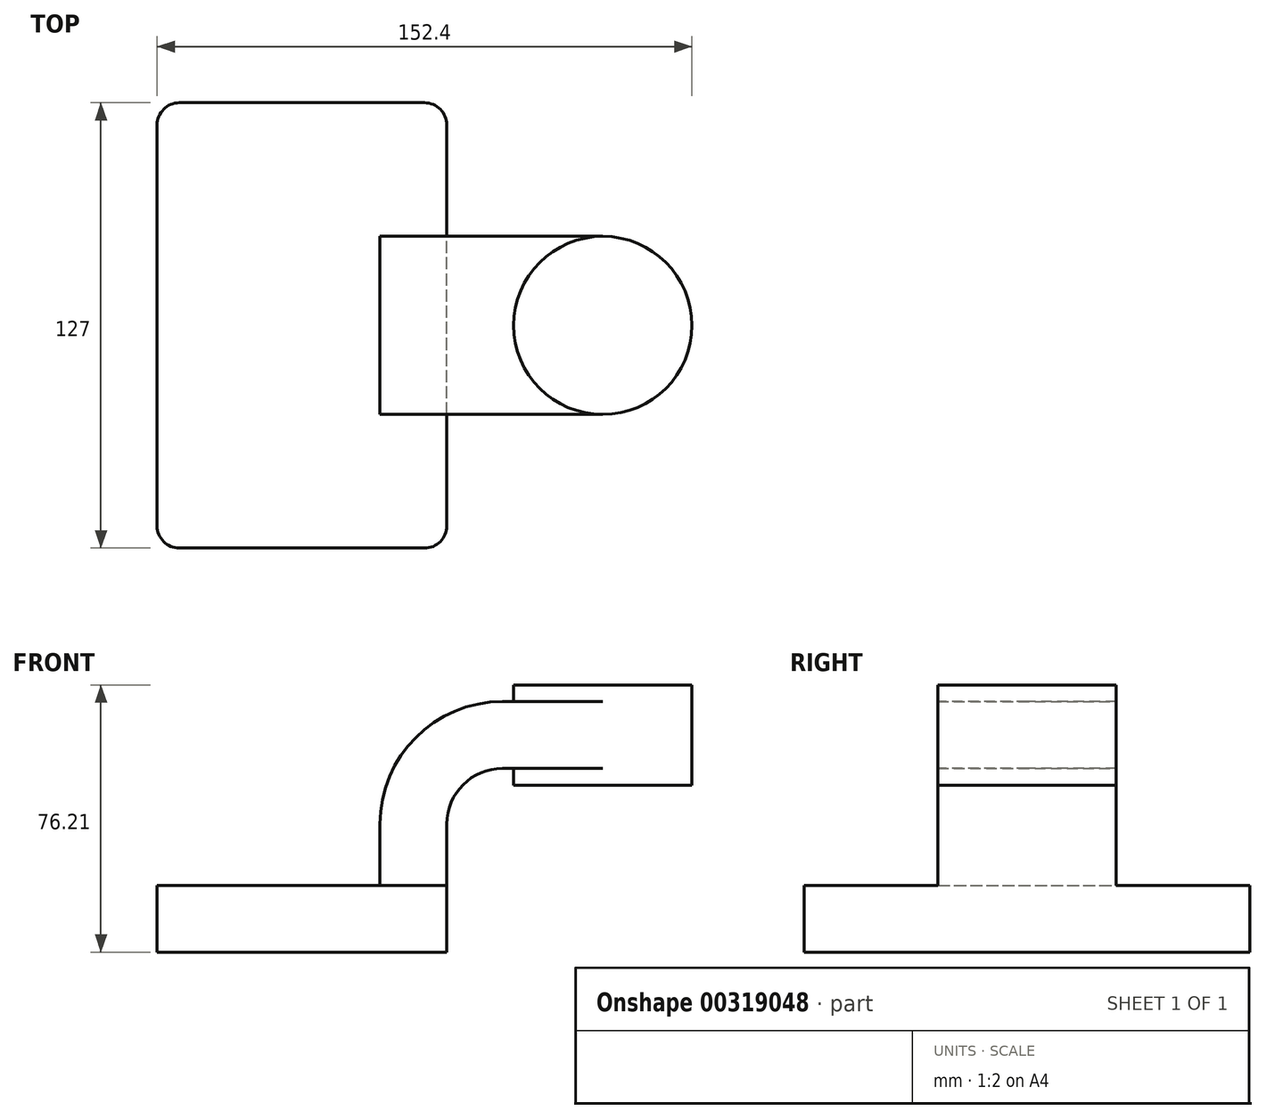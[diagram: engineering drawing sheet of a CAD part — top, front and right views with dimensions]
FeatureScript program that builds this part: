
annotation { "Feature Type Name" : "Feature", "Feature Type Description" : "" }
export const myFeature = defineFeature(function(context is Context, id is Id, definition is map)
    precondition{}
    {
        {
            var Q0;
            Q0=qCreatedBy(makeId("Front.planeOp"),FACE);
            var sketch = newSketch(context, id + "F0", { "sketchPlane" : qUnion([Q0])});
            skLineSegment(sketch, "E0.bottom", {"start": v(-41.28, -9.52) * mm, "end": v(41.28, -9.52) * mm});
            skLineSegment(sketch, "E0.top", {"start": v(-41.28, 9.53) * mm, "end": v(41.28, 9.53) * mm});
            skLineSegment(sketch, "E0.left", {"start": v(-41.28, -9.52) * mm, "end": v(-41.28, 9.53) * mm});
            skLineSegment(sketch, "E0.right", {"start": v(41.28, -9.53) * mm, "end": v(41.28, 9.52) * mm});
            skPoint(sketch, "E0.middle", {"position": v(0, 0) * mm});
            skLineSegment(sketch, "E1.bottom", {"start": v(60.32, 66.67) * mm, "end": v(111.12, 66.67) * mm});
            skLineSegment(sketch, "E1.top", {"start": v(60.32, 38.1) * mm, "end": v(111.12, 38.1) * mm});
            skLineSegment(sketch, "E1.left", {"start": v(60.32, 66.67) * mm, "end": v(60.32, 38.1) * mm});
            skLineSegment(sketch, "E1.right", {"start": v(111.12, 66.67) * mm, "end": v(111.12, 38.1) * mm});
            skPoint(sketch, "E1.middle", {"position": v(85.72, 52.39) * mm});
            skLineSegment(sketch, "E2", {"start": v(57.15, 42.86) * mm, "end": v(85.72, 42.86) * mm});
            skLineSegment(sketch, "E3", {"start": v(41.28, 9.53) * mm, "end": v(41.28, 26.99) * mm});
            skArc(sketch, "E4", {"start": v(41.27, 26.99) * mm, "mid": v(45.92, 38.21) * mm, "end": v(57.15, 42.86) * mm});
            skLineSegment(sketch, "E5.0", {"start": v(57.15, 61.91) * mm, "end": v(85.73, 61.91) * mm});
            skArc(sketch, "E5.1", {"start": v(22.23, 26.99) * mm, "mid": v(32.45, 51.68) * mm, "end": v(57.15, 61.91) * mm});
            skLineSegment(sketch, "E5.2", {"start": v(22.22, 9.53) * mm, "end": v(22.22, 26.99) * mm});
            skLineSegment(sketch, "E6", {"start": v(85.73, 38.1) * mm, "end": v(85.73, 66.67) * mm});
            skFitSpline(sketch, "E7", {"points": [v(-41.28, 9.53) * mm, v(57.15, 61.91) * mm], "startDerivative": vector(48.16, 57.23) * mm, "endDerivative": vector(134.15, -3.32) * mm});
            skSolve(sketch);
        }
        {
            var Q0;
            Q0=makeQuery(id+"F0.imprint","IMPRINT",FACE,{"disambiguationData":[TD([[makeQuery(id+"F0.imprint","IMPRINT",EDGE,{"derivedFrom":sQuery(id+"F0.wireOp",EDGE,"E0.bottom")}),1.0]])]});
            extrude(context, id + "F1", {"entities" : qUnion([Q0]), "endBound" : BoundingType.SYMMETRIC, "depth" : 127 * mm});
        }
        {
            var Q0;
            {var subQ4=sQuery(id+"F0.wireOp",EDGE,"E3");Q0=makeQuery(id+"F0.imprint","IMPRINT",FACE,{"disambiguationData":[TD([[makeQuery(id+"F0.imprint","IMPRINT",EDGE,{"derivedFrom":subQ4}),1.0]])]});}
            var Q1;
            {var subQ0=sQuery(id+"F0.wireOp",EDGE,"E5.0");var subQ1=sQuery(id+"F0.wireOp",EDGE,"E1.left");var subQ2=makeQuery(id+"F0.imprint","INTERSECT",VERTEX,{"derivedFrom":[subQ1,subQ0]});Q1=makeQuery(id+"F0.imprint","IMPRINT",FACE,{"disambiguationData":[TD([[makeQuery(id+"F0.imprint","IMPRINT",EDGE,{"disambiguationData":[TD([[subQ2,-1.0]])],"derivedFrom":subQ1}),1.0]])]});}
            extrude(context, id + "F2", {"entities" : qUnion([Q0, Q1]), "operationType" : NewBodyOperationType.ADD, "endBound" : BoundingType.SYMMETRIC, "depth" : 50.8 * mm});
        }
        {
            var Q0;
            Q0=makeQuery(id+"F0.imprint","IMPRINT",FACE,{"disambiguationData":[TD([[makeQuery(id+"F0.imprint","IMPRINT",EDGE,{"derivedFrom":sQuery(id+"F0.wireOp",EDGE,"E5.1")}),1.0]])]});
            extrude(context, id + "F3", {"entities" : qUnion([Q0]), "operationType" : NewBodyOperationType.ADD, "endBound" : BoundingType.SYMMETRIC, "depth" : 15.88 * mm});
        }
        {
            var Q0;
            {var subQ0=sQuery(id+"F0.wireOp",EDGE,"E1.right");Q0=makeQuery(id+"F0.imprint","IMPRINT",FACE,{"disambiguationData":[TD([[makeQuery(id+"F0.imprint","IMPRINT",EDGE,{"derivedFrom":subQ0}),-1.0]])]});}
            var Q1;
            Q1=sQuery(id+"F0.wireOp",EDGE,"E6");
            revolve(context, id + "F4", {"operationType" : NewBodyOperationType.ADD, "entities" : qUnion([Q0]), "axis" : qUnion([Q1]), "revolveType" : RevolveType.FULL});
        }
        {
            var Q0;
            Q0=makeQuery(id+"F1.opExtrude","CAP_EDGE",EDGE,{"disambiguationData":[OSD([sQuery(id+"F0.wireOp",EDGE,"E0.right")])],"isStart":false});
            var Q1;
            Q1=makeQuery(id+"F1.opExtrude","CAP_EDGE",EDGE,{"disambiguationData":[OSD([sQuery(id+"F0.wireOp",EDGE,"E0.left")])],"isStart":false});
            var Q2;
            Q2=makeQuery(id+"F1.opExtrude","CAP_EDGE",EDGE,{"disambiguationData":[OSD([sQuery(id+"F0.wireOp",EDGE,"E0.right")])],"isStart":true});
            var Q3;
            Q3=makeQuery(id+"F1.opExtrude","CAP_EDGE",EDGE,{"disambiguationData":[OSD([sQuery(id+"F0.wireOp",EDGE,"E0.left")])],"isStart":true});
            fillet(context, id + "F5", {"entities" : qUnion([Q0, Q1, Q2, Q3]), "radius" : 6.35 * mm, "tangentPropagation" : true, "allowEdgeOverflow" : false});
        }
    });
